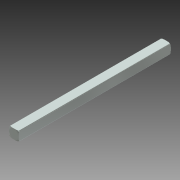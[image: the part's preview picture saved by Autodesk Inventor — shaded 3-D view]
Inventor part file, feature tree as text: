
AUTODESK INVENTOR PART (.ipt)
format: ipt  version: 2015 (Build 190159000, 159)  size: 162,816 bytes
history: native  units: in
note: dims shown in document units (in); Inventor stores cm internally (conversion verified against a paired STEP export)
features: sketch x2, plane x2, extrude x1, revolve x1, mirror x1, other x1
ambient origin geometry x8: Origin, YZ Plane, XZ Plane, XY Plane, X Axis, Y Axis, Z Axis, Center Point
bodies: Solid1 (feature_tree)
feature tree (8):
  sketch  "Sketch1"  dims[d0=2.0in d1=0.0in d2=90.0deg]
  extrude  "Extrusion1"  TaperAngle=90.0deg  [1 undecoded]
  plane  "Work Plane1"
  revolve  "Revolution1"  [1 undecoded]
  plane  "Work Plane2"
  mirror  "Mirror1"
  other  "Work Axis1"
  sketch  "Sketch2"  dims[d3=90.0deg]
note: 2 required parameter values undecoded (feature->parameter linkage not recoverable at this tier; creation-order binding heuristic only, values carry confidence <= 0.55)
